# Revit family: Haworth_LIM_Light_CL
name_source: partatom
category: Lighting Fixtures
revit_build: Autodesk Revit 2018 (Build: 20170223_1515(x64)
units: mm (PartAtom-declared; Revit-internal decimal feet)

## family parameters
Always vertical = Yes
Cut with Voids When Loaded = No
Light Source = Yes
OmniClass Number = 23.80.70.11.14
OmniClass Title = General Luminaries, Directional
Part Type = Normal
Room Calculation Point = No
Round Connector Dimension = Use Diameter
Shared = No
Work Plane-Based = No

## types (6) — shared parameters
Actual Width = 26 1/2"
Arm Length = 22"
Assembly Code = D5020200
Color Filter = 16777215
Description = Haworth LIM Light
Dimming Lamp Color Temperature Shift = <None>
Emit from Line Length = 17"
Lamp Finish = Haworth _ Metal _ Brushed Aluminum
Light Source Symbol Size = 17"
Manufacturer = Haworth
Model = LLxx-0022
Post to Centerline = 3"
Revision Number = 6
Size = Verify Final Dim. w/ Haworth
Table Thickness = 1 1/2"
URL = http://www.haworth.com
URL - Product = https://www.haworth.com
Warranty = http://www.haworth.com
Wattage Comments = 3 and 7.5 Watts 120 Volt 60 Hertz

## per-type parameters (varying)
| type | Actual Height | Add On | Add on Offset | Base | Bracket Mount | Freestanding Block | Freestanding Floor | Freestanding Pivot | Grommet Mount | Light Source Height | Min/Max Height | Stand Mount | Worksurface Mount |
| LLxx-0022 - Grommet Mount | 14" | No | 3/16" | No | Yes | No | No | No | Yes | 13 13/16" | 13-21 in. | Yes | No |
| LLxx-0022 - Freestanding Block | 14" | No | 3 1/2" | No | No | Yes | No | No | No | 13 13/16" | 13-21 in. | Yes | No |
| LLxx-0022 - Freestanding Pivot | 14" | No | 3/16" | Yes | No | No | No | Yes | No | 13 13/16" | 14-22 in. | Yes | No |
| LLxx-0022 - Freestanding Floor | 50" | No | 1" | Yes | No | No | Yes | No | No | 49 13/16" | 48-56 in. | Yes | No |
| LLxx-0022 - Worksurface Mount | 14" | No | 3/16" | No | Yes | No | No | No | No | 13 13/16" | 13-21 in. | Yes | Yes |
| LLxx-0022 - Add On | 14" | Yes | 3/16" | No | No | No | No | No | No | 3 3/4" | 13-21 in. | No | No |

## geometry (parser evidence)
native form markers: Sweep x6
no freeform markers — native parametric forms only
